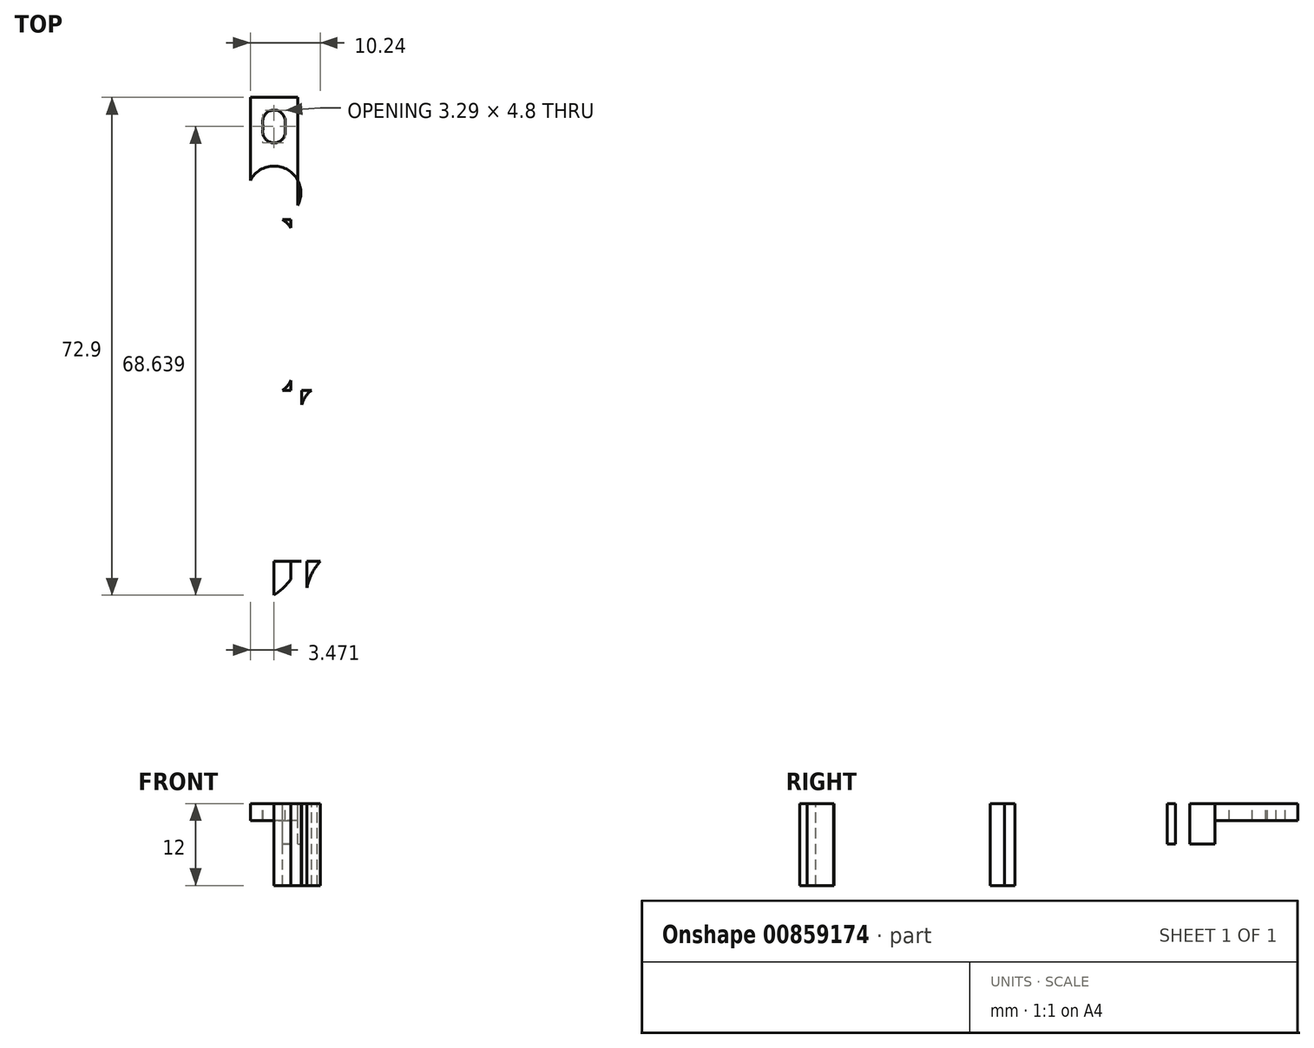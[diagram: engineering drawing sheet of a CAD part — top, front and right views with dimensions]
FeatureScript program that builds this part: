
annotation { "Feature Type Name" : "Feature", "Feature Type Description" : "" }
export const myFeature = defineFeature(function(context is Context, id is Id, definition is map)
    precondition{}
    {
        {
            var Q0;
            Q0=qCreatedBy(makeId("Top.planeOp"),FACE);
            var sketch = newSketch(context, id + "F0", { "sketchPlane" : qUnion([Q0])});
            skLineSegment(sketch, "E0.bottom", {"start": v(0, 0) * mm, "end": v(6.95, 0) * mm});
            skLineSegment(sketch, "E0.top", {"start": v(0, 17.9) * mm, "end": v(6.95, 17.9) * mm});
            skLineSegment(sketch, "E0.left", {"start": v(0, 0) * mm, "end": v(0, 17.9) * mm});
            skLineSegment(sketch, "E0.right", {"start": v(6.95, 0) * mm, "end": v(6.95, 17.9) * mm});
            skLineSegment(sketch, "E1", {"start": v(0, 0) * mm, "end": v(0, 7.85) * mm});
            skLineSegment(sketch, "E2", {"start": v(3.48, 0) * mm, "end": v(3.48, 7.85) * mm});
            skLineSegment(sketch, "E3", {"start": v(3.48, 7.85) * mm, "end": v(3.48, 6.9) * mm});
            skCircle(sketch, "E4", {"center": v(3.48, 3.92) * mm, "radius": 3.92 * mm});
            skLineSegment(sketch, "E5", {"start": v(3.47, 17.9) * mm, "end": v(3.47, 16.05) * mm});
            skLineSegment(sketch, "E6", {"start": v(3.47, 16.05) * mm, "end": v(3.48, 11.75) * mm});
            skLineSegment(sketch, "E7", {"start": v(3.47, 13.9) * mm, "end": v(3.47, 16.05) * mm});
            skLineSegment(sketch, "E8", {"start": v(3.48, 11.75) * mm, "end": v(3.47, 13.9) * mm});
            skLineSegment(sketch, "E9", {"start": v(4.55, 12.83) * mm, "end": v(4.55, 14.98) * mm});
            skLineSegment(sketch, "E10.bottom", {"start": v(3.48, 0) * mm, "end": v(1.03, 0) * mm});
            skLineSegment(sketch, "E10.top", {"start": v(3.48, -100) * mm, "end": v(1.03, -100) * mm});
            skLineSegment(sketch, "E10.left", {"start": v(3.48, 0) * mm, "end": v(3.48, -100) * mm});
            skLineSegment(sketch, "E10.right", {"start": v(1.03, 0) * mm, "end": v(1.03, -100) * mm});
            skLineSegment(sketch, "E11.bottom", {"start": v(3.48, 0) * mm, "end": v(5.93, 0) * mm});
            skLineSegment(sketch, "E11.top", {"start": v(3.48, -100) * mm, "end": v(5.93, -100) * mm});
            skLineSegment(sketch, "E11.right", {"start": v(5.93, 0) * mm, "end": v(5.93, -100) * mm});
            skLineSegment(sketch, "E12", {"start": v(5.93, 0) * mm, "end": v(5.93, 1.16) * mm});
            skLineSegment(sketch, "E13", {"start": v(1.03, 0) * mm, "end": v(1.02, 1.22) * mm});
            skLineSegment(sketch, "E14.bottom", {"start": v(6.95, 0) * mm, "end": v(9.83, -0.08) * mm});
            skLineSegment(sketch, "E14.left", {"start": v(6.95, 0) * mm, "end": v(6.95, 1.5) * mm});
            skLineSegment(sketch, "E15.right", {"start": v(5.93, -0.08) * mm, "end": v(5.93, -100) * mm});
            skLineSegment(sketch, "E16", {"start": v(3.48, 0) * mm, "end": v(3.48, -12.11) * mm});
            skLineSegment(sketch, "E17", {"start": v(3.48, 0) * mm, "end": v(3.48, -25) * mm});
            skLineSegment(sketch, "E18", {"start": v(3.48, -25) * mm, "end": v(1.03, -25) * mm});
            skLineSegment(sketch, "E19", {"start": v(1.03, -25) * mm, "end": v(1.03, -25.71) * mm});
            skLineSegment(sketch, "E20", {"start": v(1.03, -25) * mm, "end": v(1.03, -30) * mm});
            skLineSegment(sketch, "E21", {"start": v(5.93, -25) * mm, "end": v(5.93, -50) * mm});
            skPoint(sketch, "E21.startSnap0", {"position": v(2.25, -25) * mm});
            skLineSegment(sketch, "E22", {"start": v(5.93, -50) * mm, "end": v(9.83, -50.04) * mm});
            skLineSegment(sketch, "E23", {"start": v(3.48, -50) * mm, "end": v(1.03, -50) * mm});
            skLineSegment(sketch, "E24", {"start": v(5.93, -25) * mm, "end": v(9.83, -25) * mm});
            skLineSegment(sketch, "E25", {"start": v(5.93, -25) * mm, "end": v(5.93, -21.38) * mm});
            skLineSegment(sketch, "E26", {"start": v(5.93, -25) * mm, "end": v(5.93, -22.99) * mm});
            skLineSegment(sketch, "E27", {"start": v(3.48, -25) * mm, "end": v(3.48, -26.23) * mm});
            skLineSegment(sketch, "E28", {"start": v(5.93, -50) * mm, "end": v(5.93, -52.01) * mm});
            skLineSegment(sketch, "E29", {"start": v(3.48, -50) * mm, "end": v(3.48, -48.78) * mm});
            skLineSegment(sketch, "E30", {"start": v(5.93, -25) * mm, "end": v(5.93, -26.95) * mm});
            skLineSegment(sketch, "E31", {"start": v(3.48, -50) * mm, "end": v(5.93, -50) * mm});
            skLineSegment(sketch, "E32", {"start": v(3.48, 0) * mm, "end": v(3.48, -1.23) * mm});
            skLineSegment(sketch, "E33", {"start": v(6.95, 0) * mm, "end": v(6.95, 1.44) * mm});
            skLineSegment(sketch, "E34", {"start": v(1.03, 0) * mm, "end": v(1.03, -0.69) * mm});
            skLineSegment(sketch, "E35", {"start": v(1.03, 0) * mm, "end": v(1.03, -1) * mm});
            skLineSegment(sketch, "E36", {"start": v(5.93, 0) * mm, "end": v(5.93, -1.23) * mm});
            skFitSpline(sketch, "E37", {"points": [v(4.7, 0) * mm, v(5.93, -1.23) * mm], "startDerivative": vector(1.66, -0.95) * mm, "endDerivative": vector(0.86, -1.52) * mm});
            skLineSegment(sketch, "E38", {"start": v(5.93, -25) * mm, "end": v(5.93, -28.9) * mm});
            skLineSegment(sketch, "E39", {"start": v(3.48, -25) * mm, "end": v(5.93, -25) * mm});
            skLineSegment(sketch, "E40", {"start": v(5.93, -25) * mm, "end": v(5.93, -22.55) * mm});
            skLineSegment(sketch, "E41", {"start": v(5.93, -50) * mm, "end": v(5.93, -47.55) * mm});
            skLineSegment(sketch, "E42.left", {"start": v(5.93, -50) * mm, "end": v(5.93, -100) * mm});
            skLineSegment(sketch, "E43", {"start": v(9.83, -0.08) * mm, "end": v(9.83, -50.04) * mm});
            skLineSegment(sketch, "E44.bottom", {"start": v(9.83, -0.08) * mm, "end": v(12.2, -0.08) * mm});
            skLineSegment(sketch, "E44.top", {"start": v(9.83, -50.08) * mm, "end": v(12.2, -50.08) * mm});
            skLineSegment(sketch, "E44.left", {"start": v(9.83, -0.08) * mm, "end": v(9.83, -50.08) * mm});
            skLineSegment(sketch, "E44.right", {"start": v(12.2, -0.08) * mm, "end": v(12.2, -50.08) * mm});
            skLineSegment(sketch, "E45.bottom", {"start": v(5.93, -50) * mm, "end": v(8.3, -50) * mm});
            skLineSegment(sketch, "E45.top", {"start": v(5.93, -100) * mm, "end": v(8.3, -100) * mm});
            skLineSegment(sketch, "E45.right", {"start": v(8.3, -50) * mm, "end": v(8.3, -100) * mm});
            skLineSegment(sketch, "E46", {"start": v(8.3, -50) * mm, "end": v(12.2, -50.08) * mm});
            skLineSegment(sketch, "E47", {"start": v(8.3, -50) * mm, "end": v(8.3, -53.9) * mm});
            skFitSpline(sketch, "E48", {"points": [v(8.3, -53.9) * mm, v(10.24, -50.04) * mm], "startDerivative": vector(0.85, 4.55) * mm, "endDerivative": vector(3.1, 3.55) * mm});
            skLineSegment(sketch, "E49", {"start": v(3.47, 13.9) * mm, "end": v(3.47, 12.9) * mm});
            skLineSegment(sketch, "E50", {"start": v(3.47, 13.9) * mm, "end": v(3.47, 14.9) * mm});
            skCircle(sketch, "E51", {"center": v(3.47, 13.4) * mm, "radius": 1.64 * mm});
            skArc(sketch, "E52", {"start": v(5.1, 14.7) * mm, "mid": v(1.83, 14.37) * mm, "end": v(5.1, 14.14) * mm});
            skLineSegment(sketch, "E53", {"start": v(3.48, 11.75) * mm, "end": v(1.27, 11.75) * mm});
            skLineSegment(sketch, "E54", {"start": v(3.48, 11.75) * mm, "end": v(5.93, 11.75) * mm});
            skLineSegment(sketch, "E55", {"start": v(3.47, 16.05) * mm, "end": v(1.21, 16.05) * mm});
            skLineSegment(sketch, "E56", {"start": v(3.47, 16.05) * mm, "end": v(5.69, 16.05) * mm});
            skLineSegment(sketch, "E57", {"start": v(5.11, 13.43) * mm, "end": v(5.1, 14.7) * mm});
            skLineSegment(sketch, "E58", {"start": v(1.84, 13.46) * mm, "end": v(1.83, 14.38) * mm});
            skLineSegment(sketch, "E59", {"start": v(9.83, -25) * mm, "end": v(12.2, -25) * mm});
            skFitSpline(sketch, "E60", {"points": [v(11.01, -0.08) * mm, v(12.2, -1.97) * mm], "startDerivative": vector(2.1, -1.32) * mm, "endDerivative": vector(0, -2.03) * mm});
            skLineSegment(sketch, "E61", {"start": v(5.93, -25) * mm, "end": v(5.93, -43) * mm});
            skLineSegment(sketch, "E62", {"start": v(5.93, -43) * mm, "end": v(9.83, -43) * mm});
            skLineSegment(sketch, "E63", {"start": v(6.95, 0) * mm, "end": v(8.95, -0.06) * mm});
            skLineSegment(sketch, "E64", {"start": v(8.95, -0.06) * mm, "end": v(8.95, -25) * mm});
            skLineSegment(sketch, "E65", {"start": v(6.95, 0) * mm, "end": v(7.95, -0.03) * mm});
            skFitSpline(sketch, "E66", {"points": [v(7.95, -0.03) * mm, v(6.95, 0.75) * mm], "startDerivative": vector(-1.3, 0.67) * mm, "endDerivative": vector(-0.63, 0.9) * mm});
            skFitSpline(sketch, "E67", {"points": [v(7.95, -0.03) * mm, v(8.95, -1) * mm], "startDerivative": vector(1.44, -0.65) * mm, "endDerivative": vector(0.55, -1.15) * mm});
            skLineSegment(sketch, "E68", {"start": v(5.93, -25) * mm, "end": v(7.53, -25) * mm});
            skLineSegment(sketch, "E69", {"start": v(7.53, -25) * mm, "end": v(7.53, -43) * mm});
            skPoint(sketch, "E69.endSnap0", {"position": v(7.88, -43) * mm});
            skFitSpline(sketch, "E70", {"points": [v(8.95, -25) * mm, v(7.53, -27.1) * mm], "startDerivative": vector(-2.11, -1.57) * mm, "endDerivative": vector(-1.16, -3.2) * mm});
            skCircle(sketch, "E71", {"center": v(3.48, 3.92) * mm, "radius": 2.77 * mm});
            skFitSpline(sketch, "E72", {"points": [v(4.7, -25) * mm, v(5.93, -23.52) * mm], "startDerivative": vector(1.9, 1.19) * mm, "endDerivative": vector(0.85, 2) * mm});
            skFitSpline(sketch, "E73", {"points": [v(4.7, -25) * mm, v(3.48, -26.23) * mm], "startDerivative": vector(-1.92, -0.79) * mm, "endDerivative": vector(-0.51, -1.86) * mm});
            skLineSegment(sketch, "E74", {"start": v(7.53, -43) * mm, "end": v(7.45, -50.02) * mm});
            skLineSegment(sketch, "E75", {"start": v(3.48, -50) * mm, "end": v(3.48, -55) * mm});
            skLineSegment(sketch, "E76", {"start": v(3.48, -55) * mm, "end": v(7.45, -55) * mm});
            skLineSegment(sketch, "E77", {"start": v(7.45, -55) * mm, "end": v(7.45, -50.02) * mm});
            skFitSpline(sketch, "E78", {"points": [v(3.48, -55) * mm, v(7.45, -50.02) * mm], "startDerivative": vector(6.1, 4.07) * mm, "endDerivative": vector(2.72, 5.79) * mm});
            skFitSpline(sketch, "E79", {"points": [v(1.03, 0) * mm, v(5.93, -7.2) * mm], "startDerivative": vector(7.35, -4.6) * mm, "endDerivative": vector(2.63, -9.63) * mm});
            skCircle(sketch, "E80", {"center": v(3.47, 12.9) * mm, "radius": 1.66 * mm});
            skLineSegment(sketch, "E81", {"start": v(10.1, -0.08) * mm, "end": v(10.1, -24.86) * mm});
            skFitSpline(sketch, "E82", {"points": [v(8.95, -25) * mm, v(10.1, -23.62) * mm], "startDerivative": vector(1.66, 1.04) * mm, "endDerivative": vector(0.84, 1.5) * mm});
            skFitSpline(sketch, "E83", {"points": [v(8.95, -0.06) * mm, v(10.1, -1.06) * mm], "startDerivative": vector(1.73, -0.63) * mm, "endDerivative": vector(0.64, -1.36) * mm});
            skFitSpline(sketch, "E84", {"points": [v(8.95, -0.06) * mm, v(7.38, 3.57) * mm], "startDerivative": vector(-3.16, 3.34) * mm, "endDerivative": vector(-0.15, 3.87) * mm});
            skSolve(sketch);
        }
        {
            var Q0;
            {var subQ0=sQuery(id+"F0.wireOp",EDGE,"E3");Q0=makeQuery(id+"F0.imprint","IMPRINT",FACE,{"disambiguationData":[TD([[makeQuery(id+"F0.imprint","IMPRINT",EDGE,{"derivedFrom":subQ0}),1.0]])]});}
            var Q1;
            {var subQ0=sQuery(id+"F0.wireOp",EDGE,"E4");var subQ1=sQuery(id+"F0.wireOp",EDGE,"E0.right");var subQ2=makeQuery(id+"F0.imprint","INTERSECT",VERTEX,{"disambiguationData":[OD(0.0)],"derivedFrom":[subQ1,subQ0]});Q1=makeQuery(id+"F0.imprint","IMPRINT",FACE,{"disambiguationData":[TD([[makeQuery(id+"F0.imprint","IMPRINT",EDGE,{"disambiguationData":[TD([[subQ2,-1.0]])],"derivedFrom":subQ1}),-1.0]])]});}
            var Q2;
            {var subQ0=sQuery(id+"F0.wireOp",EDGE,"E3");Q2=makeQuery(id+"F0.imprint","IMPRINT",FACE,{"disambiguationData":[TD([[makeQuery(id+"F0.imprint","IMPRINT",EDGE,{"derivedFrom":subQ0}),-1.0]])]});}
            var Q3;
            {var subQ0=sQuery(id+"F0.wireOp",EDGE,"E4");var subQ1=sQuery(id+"F0.wireOp",EDGE,"E1");var subQ2=makeQuery(id+"F0.imprint","INTERSECT",VERTEX,{"disambiguationData":[OD(0.0)],"derivedFrom":[subQ1,subQ0]});Q3=makeQuery(id+"F0.imprint","IMPRINT",FACE,{"disambiguationData":[TD([[makeQuery(id+"F0.imprint","IMPRINT",EDGE,{"disambiguationData":[TD([[subQ2,-1.0]])],"derivedFrom":subQ1}),1.0]])]});}
            var Q4;
            {var subQ5=sQuery(id+"F0.wireOp",EDGE,"E14.left");Q4=makeQuery(id+"F0.imprint","IMPRINT",FACE,{"disambiguationData":[TD([[makeQuery(id+"F0.imprint","IMPRINT",EDGE,{"derivedFrom":subQ5}),1.0]])]});}
            var Q5;
            {var subQ0=sQuery(id+"F0.wireOp",EDGE,"E1");var subQ1=sQuery(id+"F0.wireOp",EDGE,"E0.bottom");var subQ2=makeQuery(id+"F0.imprint","INTERSECT",VERTEX,{"derivedFrom":[subQ1,subQ0]});Q5=makeQuery(id+"F0.imprint","IMPRINT",FACE,{"disambiguationData":[TD([[makeQuery(id+"F0.imprint","IMPRINT",EDGE,{"disambiguationData":[TD([[subQ2,-1.0]])],"derivedFrom":subQ0}),-1.0]])]});}
            var Q6;
            {var subQ0=sQuery(id+"F0.wireOp",EDGE,"E10.bottom");Q6=makeQuery(id+"F0.imprint","IMPRINT",FACE,{"disambiguationData":[TD([[makeQuery(id+"F0.imprint","IMPRINT",EDGE,{"derivedFrom":subQ0}),-1.0]])]});}
            var Q7;
            {var subQ0=sQuery(id+"F0.wireOp",EDGE,"E11.bottom");var subQ5=makeQuery(id+"F0.imprint","INTERSECT",VERTEX,{"derivedFrom":[subQ0,sQuery(id+"F0.wireOp",EDGE,"E37")]});Q7=makeQuery(id+"F0.imprint","IMPRINT",FACE,{"disambiguationData":[TD([[makeQuery(id+"F0.imprint","IMPRINT",EDGE,{"disambiguationData":[TD([[subQ5,-1.0]])],"derivedFrom":subQ0}),1.0]])]});}
            var Q8;
            {var subQ3=sQuery(id+"F0.wireOp",EDGE,"E37");Q8=makeQuery(id+"F0.imprint","IMPRINT",FACE,{"disambiguationData":[TD([[makeQuery(id+"F0.imprint","IMPRINT",EDGE,{"derivedFrom":subQ3}),1.0]])]});}
            var Q9;
            {var subQ0=sQuery(id+"F0.wireOp",EDGE,"E65");Q9=makeQuery(id+"F0.imprint","IMPRINT",FACE,{"disambiguationData":[TD([[makeQuery(id+"F0.imprint","IMPRINT",EDGE,{"derivedFrom":subQ0}),1.0]])]});}
            extrude(context, id + "F1", {"entities" : qUnion([Q0, Q1, Q2, Q3, Q4, Q5, Q6, Q7, Q8, Q9]), "depth" : -5.9 * mm, "offsetDistance" : 25 * mm});
        }
        {
            var Q0;
            {var subQ9=sQuery(id+"F0.wireOp",EDGE,"E0.left");Q0=makeQuery(id+"F0.imprint","IMPRINT",FACE,{"disambiguationData":[TD([[makeQuery(id+"F0.imprint","IMPRINT",EDGE,{"derivedFrom":subQ9}),-1.0]])]});}
            extrude(context, id + "F2", {"entities" : qUnion([Q0]), "operationType" : NewBodyOperationType.ADD, "depth" : -2.5 * mm, "offsetDistance" : 25 * mm});
        }
        {
            var Q0;
            {var subQ0=sQuery(id+"F0.wireOp",EDGE,"E4");var subQ1=sQuery(id+"F0.wireOp",EDGE,"E0.right");var subQ2=makeQuery(id+"F0.imprint","INTERSECT",VERTEX,{"disambiguationData":[OD(0.0)],"derivedFrom":[subQ1,subQ0]});Q0=makeQuery(id+"F0.imprint","IMPRINT",FACE,{"disambiguationData":[TD([[makeQuery(id+"F0.imprint","IMPRINT",EDGE,{"disambiguationData":[TD([[subQ2,1.0]])],"derivedFrom":subQ1}),-1.0]])]});}
            var Q1;
            {var subQ0=sQuery(id+"F0.wireOp",EDGE,"E14.left");Q1=makeQuery(id+"F0.imprint","IMPRINT",FACE,{"disambiguationData":[TD([[makeQuery(id+"F0.imprint","IMPRINT",EDGE,{"derivedFrom":subQ0}),-1.0]])]});}
            var Q2;
            {var subQ0=sQuery(id+"F0.wireOp",EDGE,"E10.bottom");Q2=makeQuery(id+"F0.imprint","IMPRINT",FACE,{"disambiguationData":[TD([[makeQuery(id+"F0.imprint","IMPRINT",EDGE,{"derivedFrom":subQ0}),1.0]])]});}
            var Q3;
            {var subQ0=sQuery(id+"F0.wireOp",EDGE,"E32");Q3=makeQuery(id+"F0.imprint","IMPRINT",FACE,{"disambiguationData":[TD([[makeQuery(id+"F0.imprint","IMPRINT",EDGE,{"derivedFrom":subQ0}),1.0]])]});}
            extrude(context, id + "F3", {"entities" : qUnion([Q0, Q1, Q2, Q3]), "operationType" : NewBodyOperationType.ADD, "depth" : -5.9 * mm, "offsetDistance" : 25 * mm});
        }
        {
            var Q0;
            {var subQ1=sQuery(id+"F0.wireOp",EDGE,"E25");Q0=makeQuery(id+"F0.imprint","IMPRINT",FACE,{"disambiguationData":[TD([[makeQuery(id+"F0.imprint","IMPRINT",EDGE,{"derivedFrom":subQ1}),-1.0]])]});}
            var Q1;
            {var subQ0=sQuery(id+"F0.wireOp",EDGE,"E63");Q1=makeQuery(id+"F0.imprint","IMPRINT",FACE,{"disambiguationData":[TD([[makeQuery(id+"F0.imprint","IMPRINT",EDGE,{"derivedFrom":subQ0}),-1.0]])]});}
            var Q2;
            {var subQ3=sQuery(id+"F0.wireOp",EDGE,"E44.left");var subQ5=sQuery(id+"F0.wireOp",EDGE,"E83");var subQ8=makeQuery(id+"F0.imprint","INTERSECT",VERTEX,{"derivedFrom":[subQ3,subQ5]});Q2=makeQuery(id+"F0.imprint","IMPRINT",FACE,{"disambiguationData":[TD([[makeQuery(id+"F0.imprint","IMPRINT",EDGE,{"disambiguationData":[TD([[subQ8,-1.0]])],"derivedFrom":subQ3}),-1.0]])]});}
            var Q3;
            {var subQ0=sQuery(id+"F0.wireOp",EDGE,"E83");var subQ1=sQuery(id+"F0.wireOp",EDGE,"E44.left");var subQ2=makeQuery(id+"F0.imprint","INTERSECT",VERTEX,{"derivedFrom":[subQ1,subQ0]});Q3=makeQuery(id+"F0.imprint","IMPRINT",FACE,{"disambiguationData":[TD([[makeQuery(id+"F0.imprint","IMPRINT",EDGE,{"disambiguationData":[TD([[subQ2,-1.0]])],"derivedFrom":subQ1}),1.0]])]});}
            var Q4;
            {var subQ8=sQuery(id+"F0.wireOp",EDGE,"E68");Q4=makeQuery(id+"F0.imprint","IMPRINT",FACE,{"disambiguationData":[TD([[makeQuery(id+"F0.imprint","IMPRINT",EDGE,{"derivedFrom":subQ8}),-1.0]])]});}
            var Q5;
            {var subQ4=sQuery(id+"F0.wireOp",EDGE,"E21");Q5=makeQuery(id+"F0.imprint","IMPRINT",FACE,{"disambiguationData":[TD([[makeQuery(id+"F0.imprint","IMPRINT",EDGE,{"derivedFrom":subQ4}),-1.0]])]});}
            var Q6;
            {var subQ3=sQuery(id+"F0.wireOp",EDGE,"E72");Q6=makeQuery(id+"F0.imprint","IMPRINT",FACE,{"disambiguationData":[TD([[makeQuery(id+"F0.imprint","IMPRINT",EDGE,{"derivedFrom":subQ3}),-1.0]])]});}
            var Q7;
            {var subQ3=sQuery(id+"F0.wireOp",EDGE,"E70");Q7=makeQuery(id+"F0.imprint","IMPRINT",FACE,{"disambiguationData":[TD([[makeQuery(id+"F0.imprint","IMPRINT",EDGE,{"derivedFrom":subQ3}),-1.0]])]});}
            var Q8;
            {var subQ5=sQuery(id+"F0.wireOp",EDGE,"E21");Q8=makeQuery(id+"F0.imprint","IMPRINT",FACE,{"disambiguationData":[TD([[makeQuery(id+"F0.imprint","IMPRINT",EDGE,{"derivedFrom":subQ5}),1.0]])]});}
            var Q9;
            {var subQ5=sQuery(id+"F0.wireOp",EDGE,"E31");Q9=makeQuery(id+"F0.imprint","IMPRINT",FACE,{"disambiguationData":[TD([[makeQuery(id+"F0.imprint","IMPRINT",EDGE,{"derivedFrom":subQ5}),-1.0]])]});}
            var Q10;
            {var subQ0=sQuery(id+"F0.wireOp",EDGE,"E42.left");var subQ5=makeQuery(id+"F0.imprint","IMPRINT",VERTEX,{"derivedFrom":subQ0});Q10=makeQuery(id+"F0.imprint","IMPRINT",FACE,{"disambiguationData":[TD([[makeQuery(id+"F0.imprint","IMPRINT",EDGE,{"disambiguationData":[TD([[subQ5,-1.0]])],"derivedFrom":subQ0}),1.0]])]});}
            extrude(context, id + "F4", {"entities" : qUnion([Q0, Q1, Q2, Q3, Q4, Q5, Q6, Q7, Q8, Q9, Q10]), "operationType" : NewBodyOperationType.ADD, "depth" : -12 * mm, "offsetDistance" : 25 * mm});
        }
        {
            var Q0;
            {var subQ0=sQuery(id+"F0.wireOp",EDGE,"E45.bottom");var subQ3=sQuery(id+"F0.wireOp",EDGE,"E74");var subQ5=makeQuery(id+"F0.imprint","INTERSECT",VERTEX,{"derivedFrom":[subQ0,subQ3]});Q0=makeQuery(id+"F0.imprint","IMPRINT",FACE,{"disambiguationData":[TD([[makeQuery(id+"F0.imprint","IMPRINT",EDGE,{"disambiguationData":[TD([[subQ5,-1.0]])],"derivedFrom":subQ3}),-1.0]])]});}
            extrude(context, id + "F5", {"entities" : qUnion([Q0]), "operationType" : NewBodyOperationType.ADD, "depth" : -12 * mm, "offsetDistance" : 25 * mm});
        }
    });
